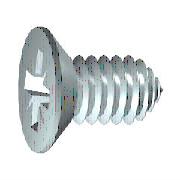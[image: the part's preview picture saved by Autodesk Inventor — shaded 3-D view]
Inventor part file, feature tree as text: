
AUTODESK INVENTOR PART (.ipt)
format: ipt  version: 2020 (Build 240168000, 168)  size: 261,632 bytes
history: native  units: mm (DEFAULTED — no unit token found)
features: extrude x2, plane x1, sketch x1
ambient origin geometry x8: Origin, YZ Plane, XZ Plane, XY Plane, X Axis, Y Axis, Z Axis, Center Point
bodies: Solid1 (feature_tree), Body (feature_tree)
feature tree (4):
  extrude  "Slot"  TaperAngle=45.0deg  [1 undecoded]
  extrude  "Star Cut"  Depth=2.2mm
  plane  "Work Plane2"
  sketch  "Sketch3"  dims[d0=32.0mm d2=45.0deg d3=4.2mm d5=8.4mm d6=4.4mm d7=4.625123mm d8=10.821041mm d9=2.51mm d16=90.0deg d10=45.0deg d11=1.76mm d12=4.4mm d13=0.515mm d14=4.4mm d15=45.0deg d17=0.515mm d18=2.6mm d19=-5.235988mm d20=29.4mm d21=0.0mm d22=2.1mm d23=3.7mm d25=0.0mm d26=2.2mm d66=25.4mm d27=0.872665mm d28=0.206mm d29=2.6mm d71=45.0deg d73=0.0mm d74=0.0mm]
note: 1 required parameter value undecoded (feature->parameter linkage not recoverable at this tier; creation-order binding heuristic only, values carry confidence <= 0.55)
